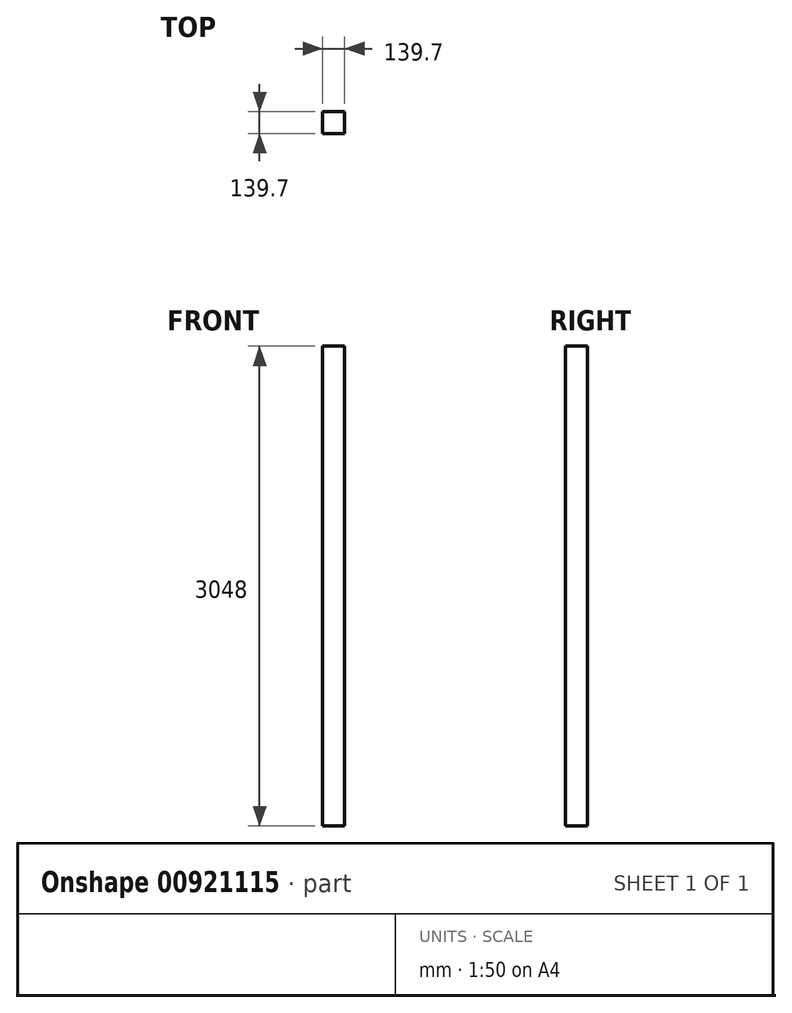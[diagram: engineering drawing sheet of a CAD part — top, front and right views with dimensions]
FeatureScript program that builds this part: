
annotation { "Feature Type Name" : "Feature", "Feature Type Description" : "" }
export const myFeature = defineFeature(function(context is Context, id is Id, definition is map)
    precondition{}
    {
        {
            var Q0;
            Q0=qCreatedBy(makeId("Top.planeOp"),FACE);
            var sketch = newSketch(context, id + "F0", { "sketchPlane" : qUnion([Q0])});
            skLineSegment(sketch, "E0.bottom", {"start": v(0, 40.07) * mm, "end": v(139.7, 40.07) * mm});
            skLineSegment(sketch, "E0.top", {"start": v(0, -99.63) * mm, "end": v(139.7, -99.63) * mm});
            skLineSegment(sketch, "E0.left", {"start": v(0, 40.07) * mm, "end": v(0, -99.63) * mm});
            skLineSegment(sketch, "E0.right", {"start": v(139.7, 40.07) * mm, "end": v(139.7, -99.63) * mm});
            skSolve(sketch);
        }
        {
            var Q0;
            Q0=qSketchRegion(id+"F0",true);
            extrude(context, id + "F1", {"entities" : qUnion([Q0]), "depth" : 3048 * mm, "offsetDistance" : 25.4 * mm});
        }
    });
